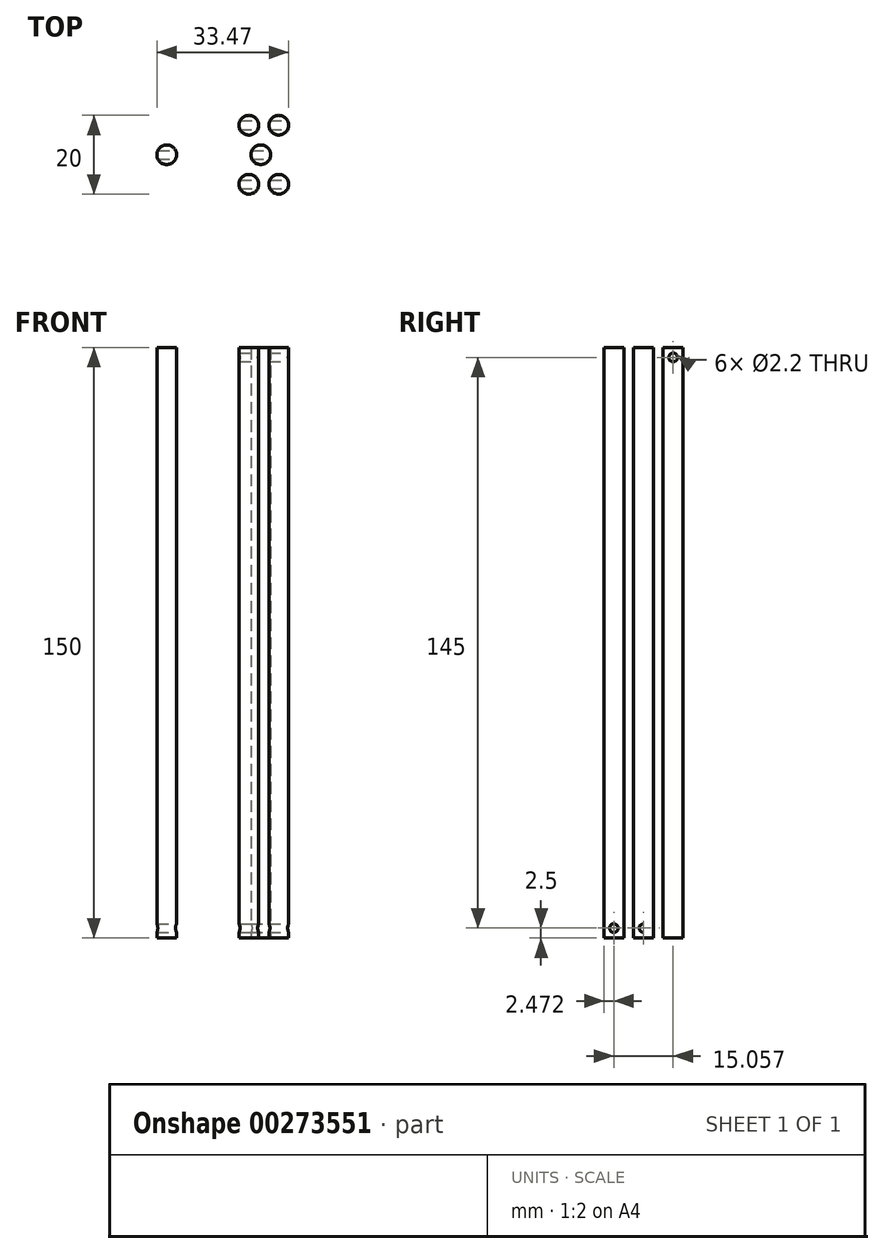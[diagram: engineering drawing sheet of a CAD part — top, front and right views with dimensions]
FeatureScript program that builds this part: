
annotation { "Feature Type Name" : "Feature", "Feature Type Description" : "" }
export const myFeature = defineFeature(function(context is Context, id is Id, definition is map)
    precondition{}
    {
        {
            var Q0;
            Q0=qCreatedBy(makeId("Top.planeOp"),FACE);
            var sketch = newSketch(context, id + "F0", { "sketchPlane" : qUnion([Q0])});
            skCircle(sketch, "E0", {"center": v(0, 0) * mm, "radius": 2.5 * mm});
            skCircle(sketch, "E1", {"center": v(-3.03, -7.5) * mm, "radius": 2.5 * mm});
            skCircle(sketch, "E2.0.1.0", {"center": v(-3.03, 7.5) * mm, "radius": 2.5 * mm});
            skCircle(sketch, "E2.1.0.0", {"center": v(4.57, -7.5) * mm, "radius": 2.5 * mm});
            skCircle(sketch, "E2.1.1.0", {"center": v(4.57, 7.5) * mm, "radius": 2.5 * mm});
            skLineSegment(sketch, "E2.direction1", {"start": v(-3.03, -7.5) * mm, "end": v(4.57, -7.5) * mm, "construction": true});
            skLineSegment(sketch, "E2.direction2", {"start": v(-3.03, -7.5) * mm, "end": v(-3.03, 7.5) * mm, "construction": true});
            skSolve(sketch);
        }
        {
            var Q0;
            Q0=makeQuery(id+"F0.imprint","IMPRINT",FACE,{"disambiguationData":[TD([[makeQuery(id+"F0.imprint","IMPRINT",EDGE,{"derivedFrom":sQuery(id+"F0.wireOp",EDGE,"E1")}),1.0]])]});
            var Q1;
            Q1=makeQuery(id+"F0.imprint","IMPRINT",FACE,{"disambiguationData":[TD([[makeQuery(id+"F0.imprint","IMPRINT",EDGE,{"derivedFrom":sQuery(id+"F0.wireOp",EDGE,"E2.0.1.0")}),1.0]])]});
            var Q2;
            Q2=makeQuery(id+"F0.imprint","IMPRINT",FACE,{"disambiguationData":[TD([[makeQuery(id+"F0.imprint","IMPRINT",EDGE,{"derivedFrom":sQuery(id+"F0.wireOp",EDGE,"E2.1.0.0")}),1.0]])]});
            var Q3;
            Q3=makeQuery(id+"F0.imprint","IMPRINT",FACE,{"disambiguationData":[TD([[makeQuery(id+"F0.imprint","IMPRINT",EDGE,{"derivedFrom":sQuery(id+"F0.wireOp",EDGE,"E2.1.1.0")}),1.0]])]});
            var Q4;
            Q4=makeQuery(id+"F0.imprint","IMPRINT",FACE,{"disambiguationData":[TD([[makeQuery(id+"F0.imprint","IMPRINT",EDGE,{"derivedFrom":sQuery(id+"F0.wireOp",EDGE,"E0")}),1.0]])]});
            extrude(context, id + "F1", {"entities" : qUnion([Q0, Q1, Q2, Q3, Q4]), "depth" : 150 * mm});
        }
        {
            var Q0;
            Q0=qCreatedBy(makeId("Right.planeOp"),FACE);
            cPlane(context, id + "F2", {"entities" : qUnion([Q0]), "cplaneType" : CPlaneType.OFFSET, "offset" : 26.8 * mm, "width" : 150 * mm, "height" : 150 * mm});
        }
        {
            var Q0;
            Q0=qCreatedBy(id+"F2.planeOp",FACE);
            var sketch = newSketch(context, id + "F3", { "sketchPlane" : qUnion([Q0])});
            skCircle(sketch, "E3", {"center": v(-7.53, 2.5) * mm, "radius": 1.1 * mm});
            skLineSegment(sketch, "E4.0", {"start": v(-10, 0) * mm, "end": v(-5, 0) * mm, "construction": true});
            skLineSegment(sketch, "E5", {"start": v(-7.5, 0) * mm, "end": v(-7.53, 2.5) * mm, "construction": true});
            skLineSegment(sketch, "E6.MirrorCS", {"start": v(10, 0) * mm, "end": v(5, 0) * mm, "construction": true});
            skLineSegment(sketch, "E7.MirrorCS", {"start": v(7.5, 0) * mm, "end": v(7.53, 2.5) * mm, "construction": true});
            skCircle(sketch, "E8.MirrorC", {"center": v(7.53, 2.5) * mm, "radius": 1.1 * mm});
            skCircle(sketch, "E9", {"center": v(0, 2.5) * mm, "radius": 1.1 * mm});
            skLineSegment(sketch, "E10", {"start": v(0, 0) * mm, "end": v(0, 75) * mm, "construction": true});
            skLineSegment(sketch, "E11", {"start": v(0, 75) * mm, "end": v(19.1, 75) * mm, "construction": true});
            skCircle(sketch, "E12.MirrorC", {"center": v(7.53, 147.5) * mm, "radius": 1.1 * mm});
            skLineSegment(sketch, "E13.MirrorCS", {"start": v(7.5, 150) * mm, "end": v(7.53, 147.5) * mm, "construction": true});
            skLineSegment(sketch, "E14.MirrorCS", {"start": v(10, 150) * mm, "end": v(5, 150) * mm, "construction": true});
            skCircle(sketch, "E15.MirrorC", {"center": v(-7.53, 147.5) * mm, "radius": 1.1 * mm});
            skCircle(sketch, "E16.MirrorC", {"center": v(0, 147.5) * mm, "radius": 1.1 * mm});
            skLineSegment(sketch, "E17.MirrorCS", {"start": v(-10, 150) * mm, "end": v(-5, 150) * mm, "construction": true});
            skLineSegment(sketch, "E18.MirrorCS", {"start": v(-7.5, 150) * mm, "end": v(-7.53, 147.5) * mm, "construction": true});
            skSolve(sketch);
        }
        {
            var Q0;
            Q0=qCreatedBy(makeId("Top.planeOp"),FACE);
            var sketch = newSketch(context, id + "F4", { "sketchPlane" : qUnion([Q0])});
            skCircle(sketch, "E19", {"center": v(-23.9, 0) * mm, "radius": 2.5 * mm});
            skSolve(sketch);
        }
        {
            var Q0;
            Q0=makeQuery(id+"F4.imprint","IMPRINT",FACE,{"disambiguationData":[TD([[makeQuery(id+"F4.imprint","IMPRINT",EDGE,{"derivedFrom":sQuery(id+"F4.wireOp",EDGE,"E19")}),1.0]])]});
            extrude(context, id + "F5", {"entities" : qUnion([Q0]), "depth" : 150 * mm});
        }
        {
            var Q0;
            Q0=makeQuery(id+"F3.imprint","IMPRINT",FACE,{"disambiguationData":[TD([[makeQuery(id+"F3.imprint","IMPRINT",EDGE,{"derivedFrom":sQuery(id+"F3.wireOp",EDGE,"E3")}),1.0]])]});
            var Q1;
            Q1=makeQuery(id+"F3.imprint","IMPRINT",FACE,{"disambiguationData":[TD([[makeQuery(id+"F3.imprint","IMPRINT",EDGE,{"derivedFrom":sQuery(id+"F3.wireOp",EDGE,"E9")}),1.0]])]});
            var Q2;
            Q2=makeQuery(id+"F3.imprint","IMPRINT",FACE,{"disambiguationData":[TD([[makeQuery(id+"F3.imprint","IMPRINT",EDGE,{"derivedFrom":sQuery(id+"F3.wireOp",EDGE,"E8.MirrorC")}),-1.0]])]});
            var Q3;
            Q3=makeQuery(id+"F3.imprint","IMPRINT",FACE,{"disambiguationData":[TD([[makeQuery(id+"F3.imprint","IMPRINT",EDGE,{"derivedFrom":sQuery(id+"F3.wireOp",EDGE,"E12.MirrorC")}),1.0]])]});
            var Q4;
            Q4=makeQuery(id+"F3.imprint","IMPRINT",FACE,{"disambiguationData":[TD([[makeQuery(id+"F3.imprint","IMPRINT",EDGE,{"derivedFrom":sQuery(id+"F3.wireOp",EDGE,"E16.MirrorC")}),-1.0]])]});
            var Q5;
            Q5=makeQuery(id+"F3.imprint","IMPRINT",FACE,{"disambiguationData":[TD([[makeQuery(id+"F3.imprint","IMPRINT",EDGE,{"derivedFrom":sQuery(id+"F3.wireOp",EDGE,"E15.MirrorC")}),-1.0]])]});
            var Q6;
            Q6=sQuery(id+"F3.wireOp",EDGE,"E15.MirrorC");
            var Q7;
            Q7=sQuery(id+"F3.wireOp",EDGE,"E16.MirrorC");
            var Q8;
            Q8=sQuery(id+"F3.wireOp",EDGE,"E12.MirrorC");
            var Q9;
            Q9=sQuery(id+"F3.wireOp",EDGE,"E3");
            var Q10;
            Q10=sQuery(id+"F3.wireOp",EDGE,"E9");
            var Q11;
            Q11=sQuery(id+"F3.wireOp",EDGE,"E8.MirrorC");
            extrude(context, id + "F6", {"entities" : qUnion([Q0, Q1, Q2, Q3, Q4, Q5]), "operationType" : NewBodyOperationType.REMOVE, "surfaceEntities" : qUnion([Q6, Q7, Q8, Q9, Q10, Q11]), "oppositeDirection" : true, "depth" : 10000 * mm});
        }
    });
